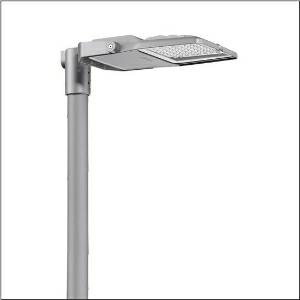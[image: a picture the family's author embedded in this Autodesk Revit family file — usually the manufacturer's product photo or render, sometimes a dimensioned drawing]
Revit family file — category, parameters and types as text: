
# Revit family: floodlight_fl_21_mini___pl33t_5xa7776b2f3a_1e67
name_source: partatom
category: Lighting Fixtures
units: mm (PartAtom-declared; Revit-internal decimal feet)

## family parameters
Cut with Voids When Loaded = No
Host = Face
Light Source = No
Part Type = Normal
Room Calculation Point = No
Round Connector Dimension = Use Diameter
Shared = No

## types (1)
- --- (1 x LED, 6150 lm, 45.7 W, 3000K)
    Apparent Load = 46 VA
    CIE Flux Codes = 26 75 99 100 100
    Color Rendering = 70
    Color Temperature = 3000K
    Default Elevation = 1800 mm
    Description = Floodlight FL 21 mini, floodlight, primary light control with lens, of PMMA, primary optical cover: protective disc, of toughened safety glass, transparent, light distribution: PL33T, light emission: direct distribution, installation type: surface-mounted, LED, High Power LED, rated luminous flux: 6.150lm, luminous efficacy: 135lm/W, light colour: 730, colour temperature: 3000K, control gear: Smart Interface (Zhaga), control: flexible luminous flux parameterisation, time-dependent luminous flux control, constant luminous flux control, overheat protection, pre-setting: logarithmic dimming characteristic, with terminal, 6-pole, mains connection: 220..240V, AC, 50/60Hz, start of lifetime: 46W, end of service life: 48W, reduction: 22W, luminaire housing, of diecast aluminium, powder-coated, SITECO metallic grey (DB 702S), corrosivity category C5 mid according to DIN EN ISO 12944, suitable for swimming pools, chlorine-resistant, sealing non-destructively replaceable, please order mast flange separately, mast bracket, of steel, galvanised, powder-coated, SITECO metallic grey (DB 702S), Smart Interface below and above, protection rating (complete): IP66, insulation class (complete): insulation class II (safety insulation), certification: CE, ENEC, VDE, protection symbol: D, impact resistance: IK08, permissible operating ambient temperature: -40..+40°C, permissible operating ambient temperature for outdoor applications: -40..+50°C, standard: DIN EN 12944, LABS conformity tested according to VDMA 24364:2018-05, packaging unit: 1 piece

Light Distribution: PL33T
    Height = 70 mm
    Lamp = 1 x LED
    Lamp Light Flux = 6150 lm
    Lamp Power = 45.7 W
    Lamp count = 1
    Length = 485 mm
    Luminous efficacy = 135 lm/W
    Manufacturer = Siteco
    ModVariant = No
    Model = 5XA7776B2F3A
    Number of Poles = 1
    OnlyDefault = Yes
    Power Factor = 1
    Product Name = Floodlight FL 21 mini | PL33T
    Product group = floodlight | pylon annexe
    ProductGroupID = 6201
    Protection Class = Protection class II
    Protection Degree = IP 66
    RLX_Detail_Level = 1
    RLX_Emergency_Light_Flux = 0 lm
    RLX_Emergency_Type = 0
    RLX_Emergency_Type_DB = No
    RlxData = <blob elided: 101033 chars, md5=f6d0ee85>
    Socket = socket
    Standby Power = 0 W
    System Light Flux = 6150 lm
    System Power = 46 W
    Type Comments = factory setting: luminous flux: 100 % | dim-lin: 254 | 463 mA
    Type Image = l_1007125.jpg
    URL = http://relux.com
    VarID = @adj_148101
    Voltage = 0 V
    Weight = 0.00 kg
    Width = 337 mm

## geometry (parser evidence)
native form markers: Blend x4, Sweep x13
no freeform markers — native parametric forms only
